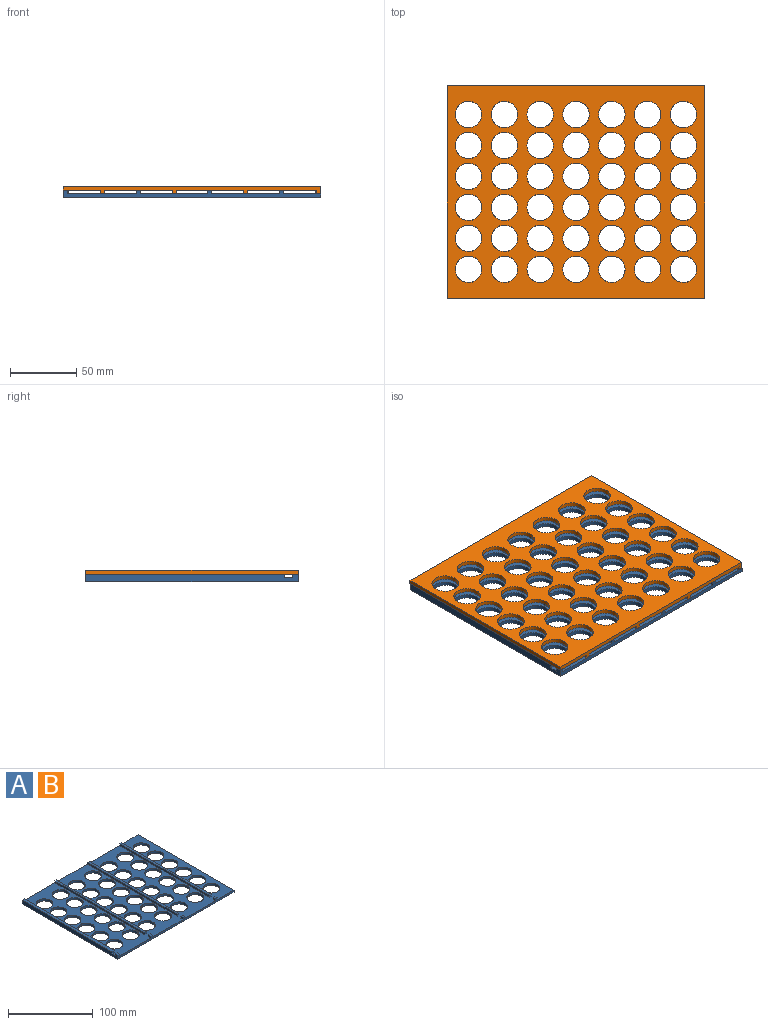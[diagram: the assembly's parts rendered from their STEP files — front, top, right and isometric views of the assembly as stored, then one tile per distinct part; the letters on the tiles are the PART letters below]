
ASSEMBLY  parts=2 mates=1
PART A: 78 faces, bbox 194x160x5.7 mm
  f0: plane 194x160mm, normal (0,0,1), area 15847.3mm2, adj f1,f2,f3,f4,f6,f7,f9,f10
  f1: plane 194x5.65mm, normal (0,1,0), area 616.5mm2, adj f0,f2,f4,f5,f10,f11,f12,f14
  f2: plane 160x5.65mm, normal (-1,0,0), area 888.1mm2, adj f0,f1,f3,f5,f6,f8,f9,f11
  f3: plane 194x5.65mm, normal (0,-1,0), area 613.8mm2, adj f0,f2,f4,f5,f7,f8,f24,f25
  f4: plane 160x3mm, normal (1,0,0), area 480mm2, adj f0,f1,f3,f5
  f5: plane 194x160mm, normal (0,0,-1), area 17845.3mm2, adj f1,f2,f3,f4,f36,f37,f38,f39
  f6: plane 3x2.65mm, normal (0,1,0), area 8mm2, adj f0,f2,f7,f8
  f7: plane 4x2.65mm, normal (1,0,0), area 10.6mm2, adj f0,f3,f6,f8
  f8: plane 4x3mm, normal (0,0,1), area 12mm2, adj f2,f3,f6,f7
  f9: plane 4x2.65mm, normal (0,-1,0), area 10.6mm2, adj f0,f2,f10,f11
  f10: plane 150x2.65mm, normal (1,0,0), area 397.5mm2, adj f0,f1,f9,f11
  f11: plane 150x4mm, normal (0,0,1), area 600mm2, adj f1,f2,f9,f10
  f12: plane 150x2.65mm, normal (-1,0,0), area 397.5mm2, adj f0,f1,f13,f15
  f13: plane 3x2.65mm, normal (0,-1,0), area 8mm2, adj f0,f12,f14,f15
  f14: plane 150x2.65mm, normal (1,0,0), area 397.5mm2, adj f0,f1,f13,f15
  f15: plane 150x3mm, normal (0,0,1), area 450mm2, adj f1,f12,f13,f14
  f16: plane 150x2.65mm, normal (-1,0,0), area 397.5mm2, adj f0,f1,f17,f19
  f17: plane 3x2.65mm, normal (0,-1,0), area 7.9mm2, adj f0,f16,f18,f19
  f18: plane 150x2.65mm, normal (1,0,0), area 397.5mm2, adj f0,f1,f17,f19
  f19: plane 150x3mm, normal (0,0,1), area 450mm2, adj f1,f16,f17,f18
  f20: plane 150x2.65mm, normal (-1,0,0), area 397.5mm2, adj f0,f1,f21,f23
  f21: plane 3x2.65mm, normal (0,-1,0), area 8mm2, adj f0,f20,f22,f23
  f22: plane 150x2.65mm, normal (1,0,0), area 397.5mm2, adj f0,f1,f21,f23
  f23: plane 150x3mm, normal (0,0,1), area 450mm2, adj f1,f20,f21,f22
  f24: plane 4x2.65mm, normal (-1,0,0), area 10.6mm2, adj f0,f3,f26,f27
  f25: plane 4x2.65mm, normal (1,0,0), area 10.6mm2, adj f0,f3,f26,f27
  f26: plane 3x2.65mm, normal (0,1,0), area 8mm2, adj f0,f24,f25,f27
  f27: plane 4x3mm, normal (0,0,1), area 12mm2, adj f3,f24,f25,f26
  f28: plane 4x2.65mm, normal (-1,0,0), area 10.6mm2, adj f0,f3,f30,f31
  f29: plane 4x2.65mm, normal (1,0,0), area 10.6mm2, adj f0,f3,f30,f31
  f30: plane 3x2.65mm, normal (0,1,0), area 7.9mm2, adj f0,f28,f29,f31
  f31: plane 4x3mm, normal (0,0,1), area 12mm2, adj f3,f28,f29,f30
  f32: plane 4x2.65mm, normal (-1,0,0), area 10.6mm2, adj f0,f3,f34,f35
  f33: plane 4x2.65mm, normal (1,0,0), area 10.6mm2, adj f0,f3,f34,f35
  f34: plane 3x2.65mm, normal (0,1,0), area 8mm2, adj f0,f32,f33,f35
  f35: plane 4x3mm, normal (0,0,1), area 12mm2, adj f3,f32,f33,f34
  f36: cylinder r=10mm len=20mm, axis (0,0,1), area 188.5mm2, adj f0,f5
  f37: cylinder r=10mm len=20mm, axis (0,0,1), area 188.5mm2, adj f0,f5
  f38: cylinder r=10mm len=20mm, axis (0,0,1), area 188.5mm2, adj f0,f5
  f39: cylinder r=10mm len=20mm, axis (0,0,1), area 188.5mm2, adj f0,f5
  f40: cylinder r=10mm len=20mm, axis (0,0,1), area 188.5mm2, adj f0,f5
  f41: cylinder r=10mm len=20mm, axis (0,0,1), area 188.5mm2, adj f0,f5
  f42: cylinder r=10mm len=20mm, axis (0,0,1), area 188.5mm2, adj f0,f5
  f43: cylinder r=10mm len=20mm, axis (0,0,1), area 188.5mm2, adj f0,f5
  f44: cylinder r=10mm len=20mm, axis (0,0,1), area 188.5mm2, adj f0,f5
  f45: cylinder r=10mm len=20mm, axis (0,0,1), area 188.5mm2, adj f0,f5
  f46: cylinder r=10mm len=20mm, axis (0,0,1), area 188.5mm2, adj f0,f5
  f47: cylinder r=10mm len=20mm, axis (0,0,1), area 188.5mm2, adj f0,f5
  f48: cylinder r=10mm len=20mm, axis (0,0,1), area 188.5mm2, adj f0,f5
  f49: cylinder r=10mm len=20mm, axis (0,0,1), area 188.5mm2, adj f0,f5
  f50: cylinder r=10mm len=20mm, axis (0,0,1), area 188.5mm2, adj f0,f5
  f51: cylinder r=10mm len=20mm, axis (0,0,1), area 188.5mm2, adj f0,f5
  f52: cylinder r=10mm len=20mm, axis (0,0,1), area 188.5mm2, adj f0,f5
  f53: cylinder r=10mm len=20mm, axis (0,0,1), area 188.5mm2, adj f0,f5
  f54: cylinder r=10mm len=20mm, axis (0,0,1), area 188.5mm2, adj f0,f5
  f55: cylinder r=10mm len=20mm, axis (0,0,1), area 188.5mm2, adj f0,f5
  f56: cylinder r=10mm len=20mm, axis (0,0,1), area 188.5mm2, adj f0,f5
  f57: cylinder r=10mm len=20mm, axis (0,0,1), area 188.5mm2, adj f0,f5
  f58: cylinder r=10mm len=20mm, axis (0,0,1), area 188.5mm2, adj f0,f5
  f59: cylinder r=10mm len=20mm, axis (0,0,1), area 188.5mm2, adj f0,f5
  f60: cylinder r=10mm len=20mm, axis (0,0,1), area 188.5mm2, adj f0,f5
  f61: cylinder r=10mm len=20mm, axis (0,0,1), area 188.5mm2, adj f0,f5
  f62: cylinder r=10mm len=20mm, axis (0,0,1), area 188.5mm2, adj f0,f5
  f63: cylinder r=10mm len=20mm, axis (0,0,1), area 188.5mm2, adj f0,f5
  f64: cylinder r=10mm len=20mm, axis (0,0,1), area 188.5mm2, adj f0,f5
  f65: cylinder r=10mm len=20mm, axis (0,0,1), area 188.5mm2, adj f0,f5
  f66: cylinder r=10mm len=20mm, axis (0,0,1), area 188.5mm2, adj f0,f5
  f67: cylinder r=10mm len=20mm, axis (0,0,1), area 188.5mm2, adj f0,f5
  f68: cylinder r=10mm len=20mm, axis (0,0,1), area 188.5mm2, adj f0,f5
  f69: cylinder r=10mm len=20mm, axis (0,0,1), area 188.5mm2, adj f0,f5
  f70: cylinder r=10mm len=20mm, axis (0,0,1), area 188.5mm2, adj f0,f5
  f71: cylinder r=10mm len=20mm, axis (0,0,1), area 188.5mm2, adj f0,f5
  f72: cylinder r=10mm len=20mm, axis (0,0,1), area 188.5mm2, adj f0,f5
  f73: cylinder r=10mm len=20mm, axis (0,0,1), area 188.5mm2, adj f0,f5
  f74: cylinder r=10mm len=20mm, axis (0,0,1), area 188.5mm2, adj f0,f5
  f75: cylinder r=10mm len=20mm, axis (0,0,1), area 188.5mm2, adj f0,f5
  f76: cylinder r=10mm len=20mm, axis (0,0,1), area 188.5mm2, adj f0,f5
  f77: cylinder r=10mm len=20mm, axis (0,0,1), area 188.5mm2, adj f0,f5
PART B: same geometry as A
PLACE A t=(8.57,-35.01,16.7)mm
PLACE B rot(axis=(0,1,0),180deg) t=(-2.6,-35.01,25.35)mm
MATE planar B.f8 <-> A.f0  axis (0,0,-1) through (99.98,-65.26,19.7)mm
